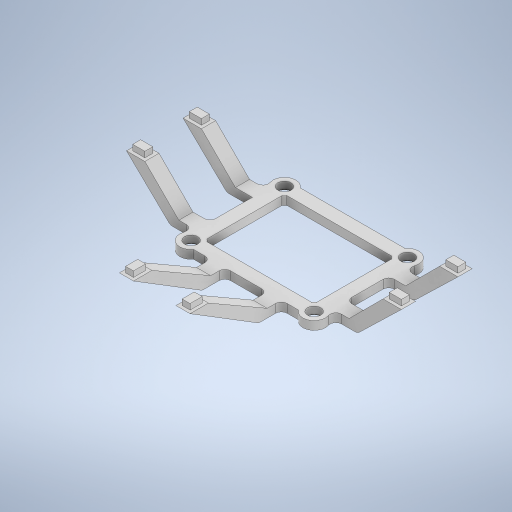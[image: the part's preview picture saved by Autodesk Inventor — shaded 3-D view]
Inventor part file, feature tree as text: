
AUTODESK INVENTOR PART (.ipt)
format: ipt  version: 2024.2 (Build 282272000, 272)  size: 465,408 bytes
history: native  units: mm
features: extrude x5, mirror x5, sketch x5, plane x4, fillet x2, chamfer x1
ambient origin geometry x8: Origin, YZ Plane, XZ Plane, XY Plane, X Axis, Y Axis, Z Axis, Center Point
bodies: Solid1 (feature_tree)
feature tree (22):
  extrude  "Extrusion1"  Depth=8.0mm
  chamfer  "Chamfer1"  Distance=4.7mm
  plane  "Work Plane2"
  extrude  "Extrusion2"  Depth=8.0mm
  plane  "Work Plane4"
  plane  "Work Plane5"
  mirror  "Mirror1"
  mirror  "Mirror2"
  plane  "Work Plane6"
  extrude  "Extrusion5"  Depth=4.0mm
  mirror  "Mirror5"
  extrude  "Extrusion4"  Depth=4.0mm
  mirror  "Mirror3"
  mirror  "Mirror4"
  extrude  "Extrusion6"  Depth=4.0mm
  fillet  "Fillet1"  Radius=4.0mm
  fillet  "Fillet2"  Radius=4.0mm
  sketch  "Sketch1"  dims[d0=4.7mm d1=8.0mm]
  sketch  "Sketch2"  dims[d2=4.7mm]
  sketch  "Sketch5"  dims[d3=8.0mm]
  sketch  "Sketch7"  dims[d4=4.7mm]
  sketch  "Sketch8"  dims[d5=8.0mm d6=4.7mm d7=8.0mm d8=4.0mm d9=4.0mm d10=4.0mm d11=4.0mm d12=4.0mm d13=4.0mm d14=4.0mm d15=4.0mm d16=33.0mm d17=4.7mm d18=4.7mm d19=4.7mm d20=4.7mm d21=2.35mm d22=2.35mm d23=2.35mm d24=2.35mm d25=43.5mm d26=3.0mm d27=0.0mm d28=0.5mm d29=2.0mm d30=45.0deg d32=4.0mm d41=5.0mm d42=0.0mm d47=21.75mm d48=16.5mm d49=6.5mm d61=9.0mm d62=4.3mm d63=2.8mm d64=1.1mm d65=1.1mm d66=2.0mm d67=0.0mm d71=9.25mm d72=8.0mm d73=6.5mm d76=5.0mm d77=0.0mm d78=2.8mm d79=4.3mm d80=2.8mm d81=4.3mm d82=1.1mm d83=1.1mm d84=1.1mm d85=1.1mm d86=2.0mm d87=0.0mm d91=6.0mm d93=45.0deg d94=15.0mm d95=15.0mm d96=2.0mm d97=2.0mm d98=5.0mm d99=30.0deg]
